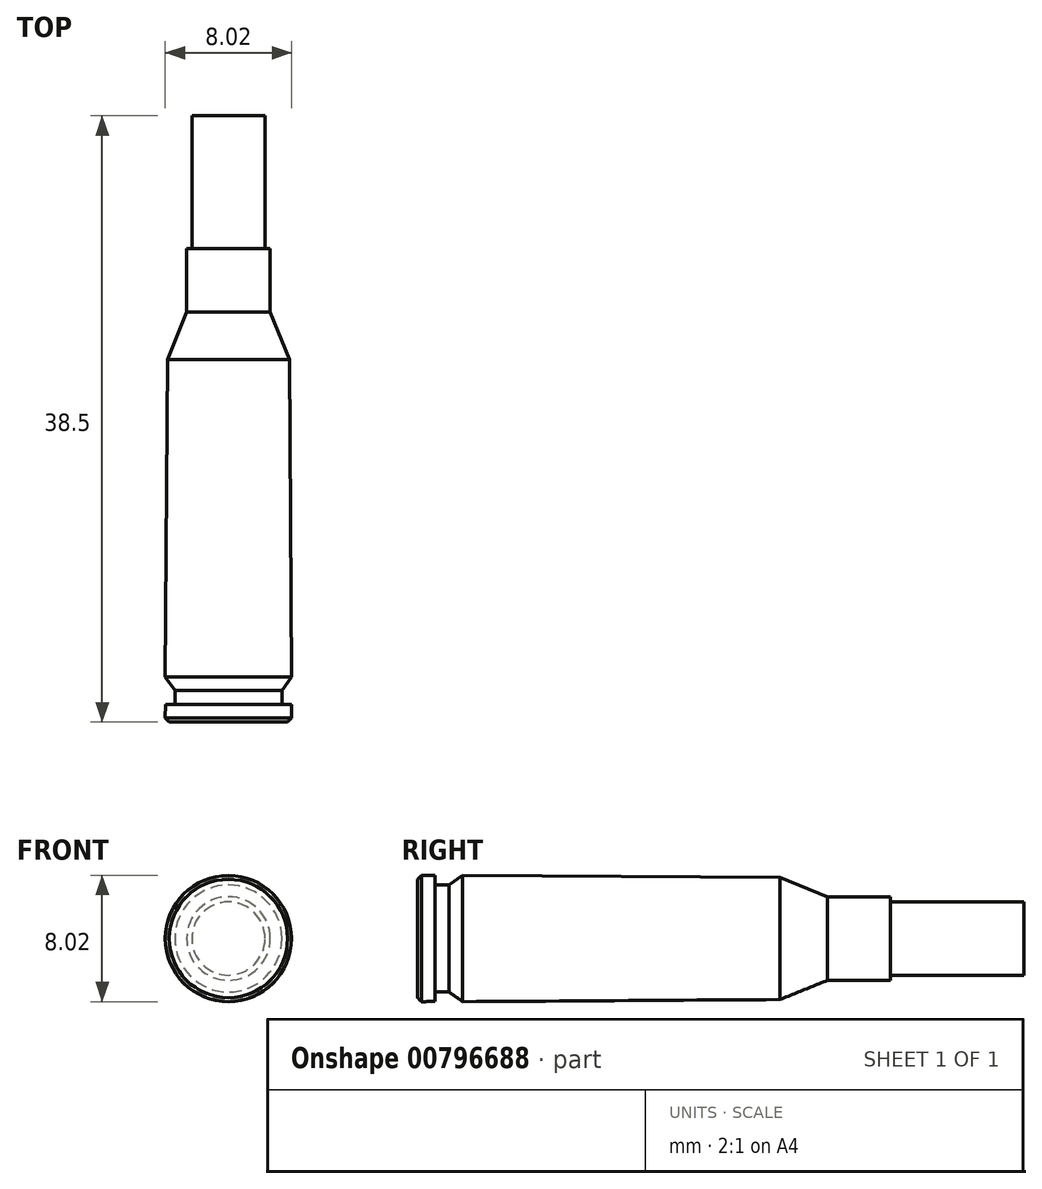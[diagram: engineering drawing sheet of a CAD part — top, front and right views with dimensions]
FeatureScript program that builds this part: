
annotation { "Feature Type Name" : "Feature", "Feature Type Description" : "" }
export const myFeature = defineFeature(function(context is Context, id is Id, definition is map)
    precondition{}
    {
        {
            var Q0;
            Q0=qCreatedBy(makeId("Right.planeOp"),FACE);
            var sketch = newSketch(context, id + "F0", { "sketchPlane" : qUnion([Q0])});
            skLineSegment(sketch, "E0", {"start": v(0, 0) * mm, "end": v(0.25, 0) * mm});
            skLineSegment(sketch, "E1", {"start": v(0, -1.69) * mm, "end": v(1.1, -1.69) * mm});
            skLineSegment(sketch, "E2", {"start": v(0.25, 0) * mm, "end": v(1.1, 0) * mm});
            skLineSegment(sketch, "E3", {"start": v(1.1, 0) * mm, "end": v(2, 0) * mm});
            skLineSegment(sketch, "E4", {"start": v(0, -2.54) * mm, "end": v(2.87, -2.54) * mm});
            skLineSegment(sketch, "E5", {"start": v(0, -3.9) * mm, "end": v(23.02, -3.9) * mm});
            skLineSegment(sketch, "E6", {"start": v(0, -5.9) * mm, "end": v(26.03, -5.9) * mm});
            skLineSegment(sketch, "E7", {"start": v(0, -8.71) * mm, "end": v(30.05, -8.71) * mm});
            skLineSegment(sketch, "E8", {"start": v(0, -11.83) * mm, "end": v(38.5, -11.83) * mm});
            skLineSegment(sketch, "E9", {"start": v(2, 0) * mm, "end": v(2.87, 0) * mm});
            skLineSegment(sketch, "E10", {"start": v(2.87, 0) * mm, "end": v(23.02, 0) * mm});
            skLineSegment(sketch, "E11", {"start": v(23.02, 0) * mm, "end": v(26.03, 0) * mm});
            skLineSegment(sketch, "E12", {"start": v(26.03, 0) * mm, "end": v(30.05, 0) * mm});
            skLineSegment(sketch, "E13", {"start": v(30.05, 0) * mm, "end": v(38.5, 0) * mm});
            skLineSegment(sketch, "E14", {"start": v(38.5, 0) * mm, "end": v(38.5, 2.33) * mm});
            skLineSegment(sketch, "E15", {"start": v(38.5, 2.33) * mm, "end": v(30.05, 2.32) * mm});
            skLineSegment(sketch, "E16", {"start": v(30.05, 0) * mm, "end": v(30.05, 2.65) * mm});
            skLineSegment(sketch, "E17", {"start": v(30.05, 2.65) * mm, "end": v(26.03, 2.65) * mm});
            skLineSegment(sketch, "E18", {"start": v(23.02, 0) * mm, "end": v(23.02, 3.88) * mm});
            skLineSegment(sketch, "E19", {"start": v(23.02, 3.88) * mm, "end": v(26.03, 2.65) * mm});
            skLineSegment(sketch, "E20", {"start": v(2.87, 0) * mm, "end": v(2.87, 4) * mm});
            skLineSegment(sketch, "E21", {"start": v(2.87, 4) * mm, "end": v(23.02, 3.88) * mm});
            skLineSegment(sketch, "E22", {"start": v(2, 0) * mm, "end": v(2, 3.4) * mm});
            skLineSegment(sketch, "E23", {"start": v(2, 3.4) * mm, "end": v(2.87, 4) * mm});
            skLineSegment(sketch, "E24", {"start": v(1.1, 0) * mm, "end": v(1.1, 4) * mm});
            skLineSegment(sketch, "E25", {"start": v(1.1, 4) * mm, "end": v(0.25, 4) * mm});
            skLineSegment(sketch, "E26", {"start": v(0.25, 4) * mm, "end": v(0, 4) * mm});
            skLineSegment(sketch, "E27", {"start": v(0.25, 4) * mm, "end": v(0, 3.76) * mm});
            skLineSegment(sketch, "E28", {"start": v(0, 3.76) * mm, "end": v(0, 0) * mm});
            skLineSegment(sketch, "E29", {"start": v(2, 3.4) * mm, "end": v(1.1, 3.4) * mm});
            skSolve(sketch);
        }
        {
            var Q0;
            Q0=makeQuery(id+"F0.imprint","IMPRINT",FACE,{"disambiguationData":[TD([[makeQuery(id+"F0.imprint","IMPRINT",EDGE,{"derivedFrom":sQuery(id+"F0.wireOp",EDGE,"E0")}),1.0]])]});
            var Q1;
            {var subQ0=sQuery(id+"F0.wireOp",EDGE,"E3");Q1=makeQuery(id+"F0.imprint","IMPRINT",FACE,{"disambiguationData":[TD([[makeQuery(id+"F0.imprint","IMPRINT",EDGE,{"derivedFrom":subQ0}),1.0]])]});}
            var Q2;
            Q2=makeQuery(id+"F0.imprint","IMPRINT",FACE,{"disambiguationData":[TD([[makeQuery(id+"F0.imprint","IMPRINT",EDGE,{"derivedFrom":sQuery(id+"F0.wireOp",EDGE,"E9")}),1.0]])]});
            var Q3;
            Q3=makeQuery(id+"F0.imprint","IMPRINT",FACE,{"disambiguationData":[TD([[makeQuery(id+"F0.imprint","IMPRINT",EDGE,{"derivedFrom":sQuery(id+"F0.wireOp",EDGE,"E10")}),1.0]])]});
            var Q4;
            Q4=makeQuery(id+"F0.imprint","IMPRINT",FACE,{"disambiguationData":[TD([[makeQuery(id+"F0.imprint","IMPRINT",EDGE,{"derivedFrom":sQuery(id+"F0.wireOp",EDGE,"E11")}),1.0]])]});
            var Q5;
            {var subQ0=sQuery(id+"F0.wireOp",EDGE,"E13");Q5=makeQuery(id+"F0.imprint","IMPRINT",FACE,{"disambiguationData":[TD([[makeQuery(id+"F0.imprint","IMPRINT",EDGE,{"derivedFrom":subQ0}),1.0]])]});}
            var Q6;
            Q6=sQuery(id+"F0.wireOp",EDGE,"E10");
            revolve(context, id + "F1", {"surfaceOperationType" : NewSurfaceOperationType.NEW, "entities" : qUnion([Q0, Q1, Q2, Q3, Q4, Q5]), "axis" : qUnion([Q6]), "revolveType" : RevolveType.FULL});
        }
    });
